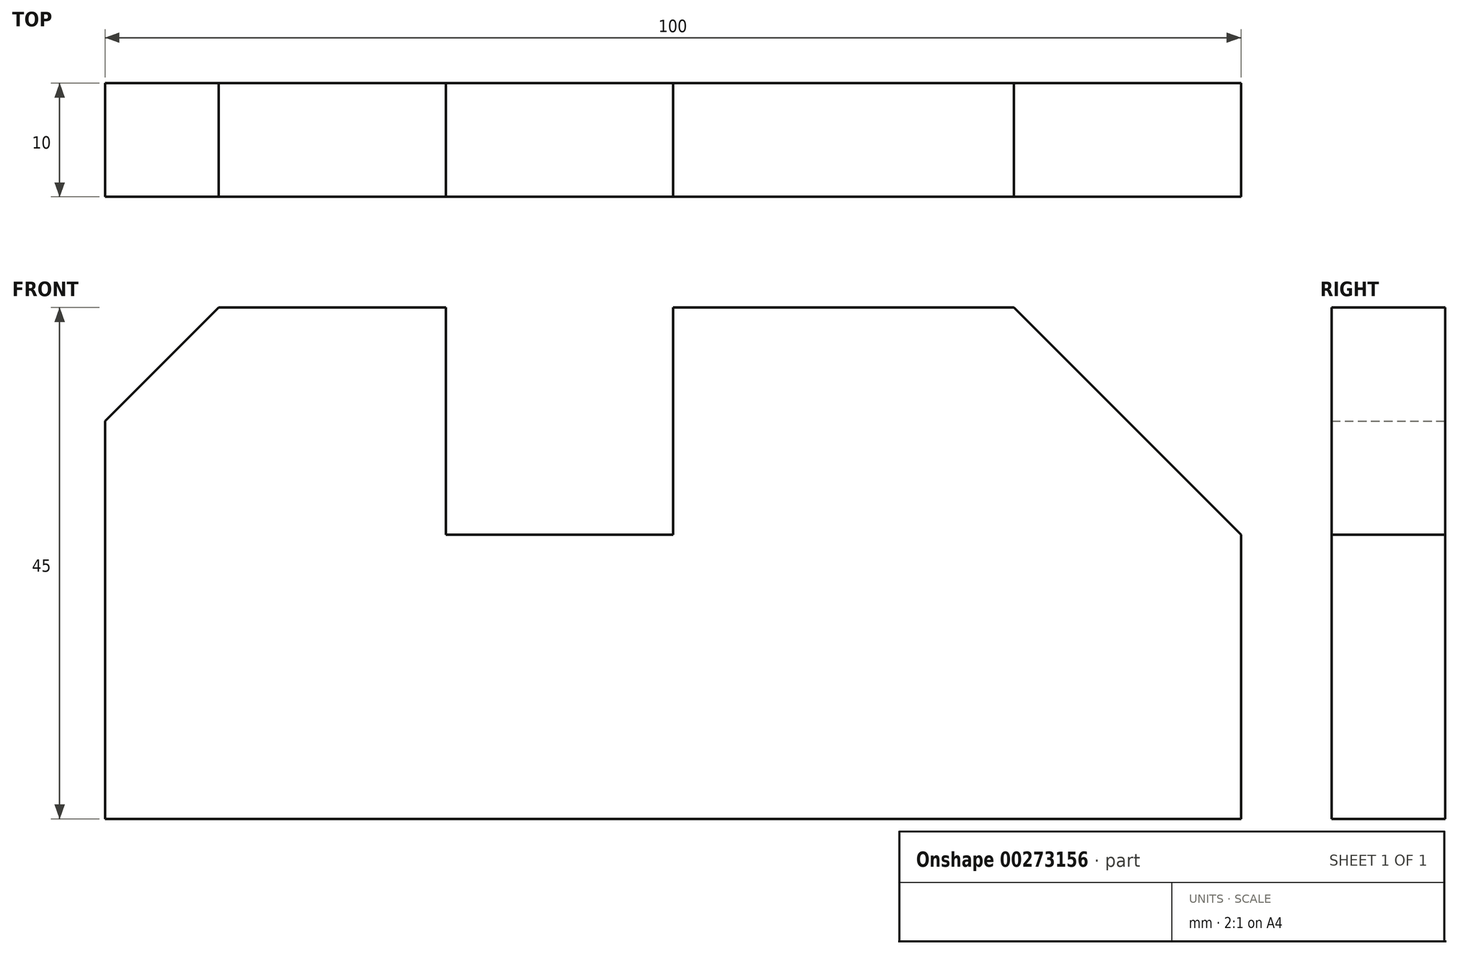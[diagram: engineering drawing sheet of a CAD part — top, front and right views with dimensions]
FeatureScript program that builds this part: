
annotation { "Feature Type Name" : "Feature", "Feature Type Description" : "" }
export const myFeature = defineFeature(function(context is Context, id is Id, definition is map)
    precondition{}
    {
        {
            var Q0;
            Q0=qCreatedBy(makeId("Front.planeOp"),FACE);
            var sketch = newSketch(context, id + "F0", { "sketchPlane" : qUnion([Q0])});
            skLineSegment(sketch, "E0", {"start": v(0, 0) * mm, "end": v(0, 35) * mm});
            skLineSegment(sketch, "E1", {"start": v(0, 35) * mm, "end": v(10, 45) * mm});
            skLineSegment(sketch, "E2", {"start": v(10, 45) * mm, "end": v(30, 45) * mm});
            skLineSegment(sketch, "E3", {"start": v(30, 45) * mm, "end": v(30, 25) * mm});
            skLineSegment(sketch, "E4", {"start": v(30, 25) * mm, "end": v(50, 25) * mm});
            skLineSegment(sketch, "E5", {"start": v(50, 25) * mm, "end": v(50, 45) * mm});
            skLineSegment(sketch, "E6", {"start": v(50, 45) * mm, "end": v(80, 45) * mm});
            skLineSegment(sketch, "E7", {"start": v(80, 45) * mm, "end": v(100, 25) * mm});
            skLineSegment(sketch, "E8", {"start": v(100, 25) * mm, "end": v(100, 0) * mm});
            skLineSegment(sketch, "E9", {"start": v(0, 0) * mm, "end": v(100, 0) * mm});
            skSolve(sketch);
        }
        {
            var Q0;
            Q0=makeQuery(id+"F0.imprint","IMPRINT",FACE,{"disambiguationData":[TD([[makeQuery(id+"F0.imprint","IMPRINT",EDGE,{"derivedFrom":sQuery(id+"F0.wireOp",EDGE,"E0")}),-1.0]])]});
            extrude(context, id + "F1", {"entities" : qUnion([Q0]), "depth" : 10 * mm});
        }
    });
